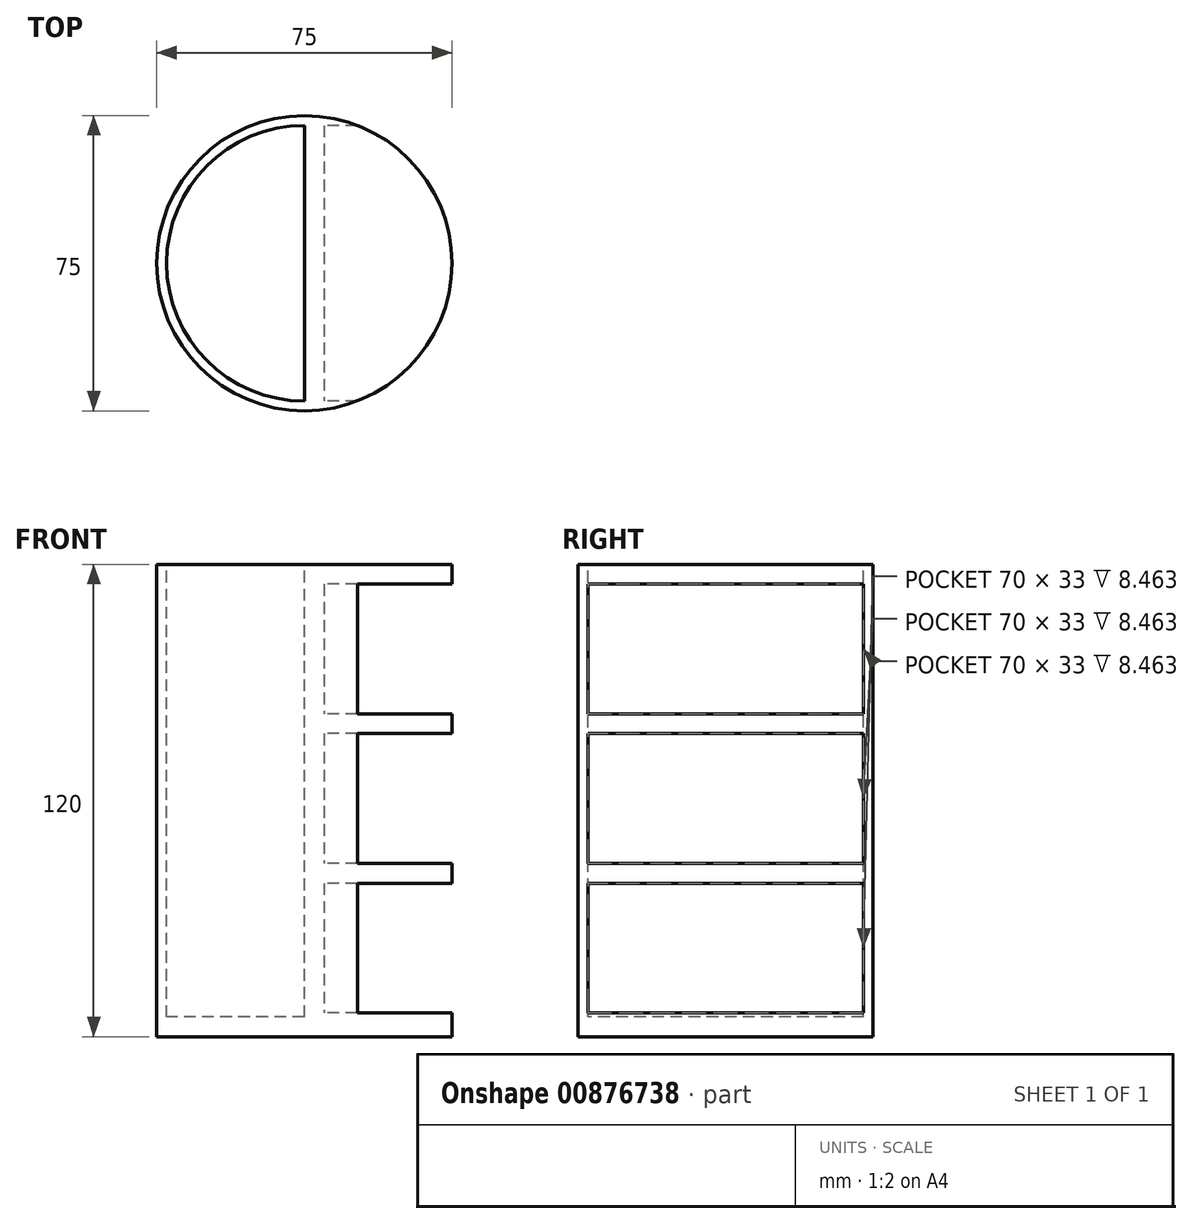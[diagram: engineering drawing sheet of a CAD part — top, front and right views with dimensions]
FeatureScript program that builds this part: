
annotation { "Feature Type Name" : "Feature", "Feature Type Description" : "" }
export const myFeature = defineFeature(function(context is Context, id is Id, definition is map)
    precondition{}
    {
        {
            var Q0;
            Q0=qCreatedBy(makeId("Top.planeOp"),FACE);
            var sketch = newSketch(context, id + "F0", { "sketchPlane" : qUnion([Q0])});
            skCircle(sketch, "E0", {"center": v(0, 0) * mm, "radius": 37.5 * mm});
            skSolve(sketch);
        }
        {
            var Q0;
            Q0=makeQuery(id+"F0.imprint","IMPRINT",FACE,{"disambiguationData":[TD([[makeQuery(id+"F0.imprint","IMPRINT",EDGE,{"derivedFrom":sQuery(id+"F0.wireOp",EDGE,"E0")}),1.0]])]});
            extrude(context, id + "F1", {"entities" : qUnion([Q0]), "depth" : 120 * mm, "offsetDistance" : 25 * mm});
        }
        {
            var Q0;
            Q0=makeQuery(id+"F1.opExtrude","CAP_FACE",FACE,{"disambiguationData":[OSD([sQuery(id+"F0.wireOp",EDGE,"E0")])],"isStart":false});
            var sketch = newSketch(context, id + "F2", { "sketchPlane" : qUnion([Q0])});
            skCircle(sketch, "E1", {"center": v(0, 0) * mm, "radius": 35 * mm});
            skLineSegment(sketch, "E2.bottom", {"start": v(35, 35) * mm, "end": v(-35, 35) * mm});
            skLineSegment(sketch, "E2.top", {"start": v(35, -35) * mm, "end": v(-35, -35) * mm});
            skLineSegment(sketch, "E2.left", {"start": v(35, 35) * mm, "end": v(35, -35) * mm});
            skLineSegment(sketch, "E2.right", {"start": v(-35, 35) * mm, "end": v(-35, -35) * mm});
            skLineSegment(sketch, "E3", {"start": v(0, 35) * mm, "end": v(0, -35) * mm});
            skLineSegment(sketch, "E4.bottom", {"start": v(0, 35) * mm, "end": v(43.98, 35) * mm});
            skLineSegment(sketch, "E4.top", {"start": v(0, 58.33) * mm, "end": v(43.98, 58.33) * mm});
            skLineSegment(sketch, "E4.left", {"start": v(0, 35) * mm, "end": v(0, 58.33) * mm});
            skLineSegment(sketch, "E4.right", {"start": v(43.98, 35) * mm, "end": v(43.98, 58.33) * mm});
            skLineSegment(sketch, "E5.bottom", {"start": v(0, -35) * mm, "end": v(63.55, -35) * mm});
            skLineSegment(sketch, "E5.top", {"start": v(0, -61.37) * mm, "end": v(63.55, -61.37) * mm});
            skLineSegment(sketch, "E5.left", {"start": v(0, -35) * mm, "end": v(0, -61.37) * mm});
            skLineSegment(sketch, "E5.right", {"start": v(63.55, -35) * mm, "end": v(63.55, -61.37) * mm});
            skSolve(sketch);
        }
        {
            var Q0;
            {var subQ0=sQuery(id+"F2.wireOp",EDGE,"E3");Q0=makeQuery(id+"F2.imprint","IMPRINT",FACE,{"disambiguationData":[TD([[makeQuery(id+"F2.imprint","IMPRINT",EDGE,{"derivedFrom":subQ0}),-1.0]])]});}
            extrude(context, id + "F3", {"entities" : qUnion([Q0]), "operationType" : NewBodyOperationType.REMOVE, "oppositeDirection" : true, "depth" : 115 * mm, "offsetDistance" : 25 * mm});
        }
        {
            var Q0;
            Q0=makeQuery(id+"F3.boolean.opBoolean","COPY",FACE,{"derivedFrom":makeQuery(id+"F3.opExtrude","SWEPT_FACE",FACE,{"disambiguationData":[OSD([sQuery(id+"F2.wireOp",EDGE,"E3")])]})});
            var sketch = newSketch(context, id + "F4", { "sketchPlane" : qUnion([Q0])});
            skLineSegment(sketch, "E6.bottom", {"start": v(35, 39) * mm, "end": v(-35, 39) * mm});
            skLineSegment(sketch, "E6.top", {"start": v(35, 6) * mm, "end": v(-35, 6) * mm});
            skLineSegment(sketch, "E6.left", {"start": v(35, 39) * mm, "end": v(35, 6) * mm});
            skLineSegment(sketch, "E6.right", {"start": v(-35, 39) * mm, "end": v(-35, 6) * mm});
            skPoint(sketch, "E6.middle", {"position": v(0, 22.5) * mm});
            skLineSegment(sketch, "E7.bottom", {"start": v(35, 77) * mm, "end": v(-35, 77) * mm});
            skLineSegment(sketch, "E7.top", {"start": v(35, 44) * mm, "end": v(-35, 44) * mm});
            skLineSegment(sketch, "E7.left", {"start": v(35, 77) * mm, "end": v(35, 44) * mm});
            skLineSegment(sketch, "E7.right", {"start": v(-35, 77) * mm, "end": v(-35, 44) * mm});
            skPoint(sketch, "E7.middle", {"position": v(0, 60.5) * mm});
            skLineSegment(sketch, "E8.bottom", {"start": v(35, 115) * mm, "end": v(-35, 115) * mm});
            skLineSegment(sketch, "E8.top", {"start": v(35, 82) * mm, "end": v(-35, 82) * mm});
            skLineSegment(sketch, "E8.left", {"start": v(35, 115) * mm, "end": v(35, 82) * mm});
            skLineSegment(sketch, "E8.right", {"start": v(-35, 115) * mm, "end": v(-35, 82) * mm});
            skPoint(sketch, "E8.middle", {"position": v(0, 98.5) * mm});
            skSolve(sketch);
        }
        {
            var Q0;
            Q0 = qSketchRegion(id + "F4", true);
            extrude(context, id + "F5", {"entities" : qUnion([Q0]), "operationType" : NewBodyOperationType.REMOVE, "oppositeDirection" : true, "depth" : 40 * mm, "offsetDistance" : 25 * mm});
        }
        {
            var Q0;
            Q0=makeQuery(id+"F5.boolean.opBoolean","COPY",FACE,{"derivedFrom":makeQuery(id+"F5.opExtrude","SWEPT_FACE",FACE,{"disambiguationData":[OSD([sQuery(id+"F4.wireOp",EDGE,"E6.top")])]})});
            var sketch = newSketch(context, id + "F6", { "sketchPlane" : qUnion([Q0])});
            skLineSegment(sketch, "E9.bottom", {"start": v(0, -35) * mm, "end": v(5, -35) * mm});
            skLineSegment(sketch, "E9.top", {"start": v(0, 35) * mm, "end": v(5, 35) * mm});
            skLineSegment(sketch, "E9.left", {"start": v(0, -35) * mm, "end": v(0, 35) * mm});
            skLineSegment(sketch, "E9.right", {"start": v(5, -35) * mm, "end": v(5, 35) * mm});
            skSolve(sketch);
        }
        {
            var Q0;
            Q0 = qSketchRegion(id + "F6", true);
            extrude(context, id + "F7", {"entities" : qUnion([Q0]), "operationType" : NewBodyOperationType.ADD, "depth" : 109 * mm, "offsetDistance" : 25 * mm});
        }
    });
